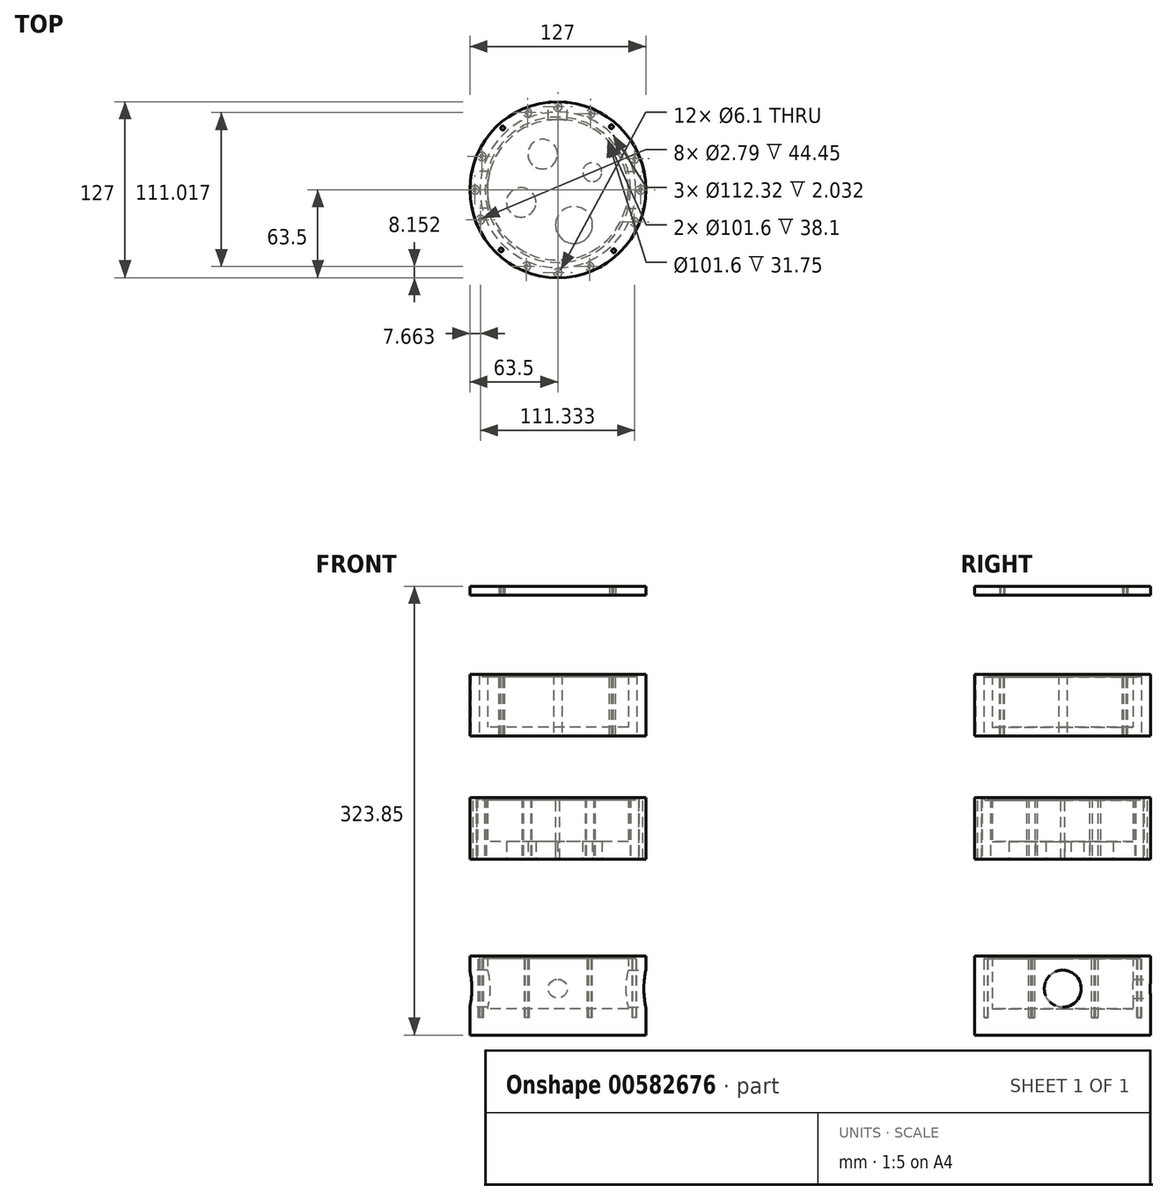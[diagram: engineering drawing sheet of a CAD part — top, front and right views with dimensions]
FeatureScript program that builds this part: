
annotation { "Feature Type Name" : "Feature", "Feature Type Description" : "" }
export const myFeature = defineFeature(function(context is Context, id is Id, definition is map)
    precondition{}
    {
        {
            var Q0;
            Q0=qCreatedBy(makeId("Top.planeOp"),FACE);
            var sketch = newSketch(context, id + "F0", { "sketchPlane" : qUnion([Q0])});
            skCircle(sketch, "E0", {"center": v(0, 0) * mm, "radius": 63.5 * mm});
            skCircle(sketch, "E1.0", {"center": v(0, 0) * mm, "radius": 50.8 * mm});
            skSolve(sketch);
        }
        {
            var Q0;
            Q0=makeQuery(id+"F0.imprint","IMPRINT",FACE,{"disambiguationData":[TD([[makeQuery(id+"F0.imprint","IMPRINT",EDGE,{"derivedFrom":sQuery(id+"F0.wireOp",EDGE,"E0")}),1.0]])]});
            extrude(context, id + "F1", {"entities" : qUnion([Q0]), "depth" : 44.45 * mm, "offsetDistance" : 25.4 * mm});
        }
        {
            var Q0;
            Q0=makeQuery(id+"F0.imprint","IMPRINT",FACE,{"disambiguationData":[TD([[makeQuery(id+"F0.imprint","IMPRINT",EDGE,{"derivedFrom":sQuery(id+"F0.wireOp",EDGE,"E1.0")}),1.0]])]});
            extrude(context, id + "F2", {"entities" : qUnion([Q0]), "operationType" : NewBodyOperationType.ADD, "depth" : 6.35 * mm, "offsetDistance" : 25.4 * mm});
        }
        {
            var Q0;
            Q0=qCreatedBy(makeId("Top.planeOp"),FACE);
            var sketch = newSketch(context, id + "F3", { "sketchPlane" : qUnion([Q0])});
            skCircle(sketch, "E2", {"center": v(0, 0) * mm, "radius": 63.5 * mm});
            skCircle(sketch, "E3.0", {"center": v(0, 0) * mm, "radius": 50.8 * mm});
            skSolve(sketch);
        }
        {
            var Q0;
            Q0=makeQuery(id+"F3.imprint","IMPRINT",FACE,{"disambiguationData":[TD([[makeQuery(id+"F3.imprint","IMPRINT",EDGE,{"derivedFrom":sQuery(id+"F3.wireOp",EDGE,"E2")}),1.0]])]});
            extrude(context, id + "F4", {"entities" : qUnion([Q0]), "operationType" : NewBodyOperationType.ADD, "depth" : 25.4 * mm, "offsetDistance" : 25.4 * mm});
        }
        {
            var Q0;
            Q0=qCreatedBy(makeId("Right.planeOp"),FACE);
            cPlane(context, id + "F5", {"entities" : qUnion([Q0]), "cplaneType" : CPlaneType.OFFSET, "offset" : 63.5 * mm, "width" : 152.4 * mm, "height" : 152.4 * mm});
        }
        {
            var Q0;
            Q0=qCreatedBy(makeId("Right.planeOp"),FACE);
            cPlane(context, id + "F6", {"entities" : qUnion([Q0]), "cplaneType" : CPlaneType.OFFSET, "offset" : 63.5 * mm, "oppositeDirection" : true, "width" : 152.4 * mm, "height" : 152.4 * mm});
        }
        {
            var Q0;
            Q0=qCreatedBy(id+"F6.planeOp",FACE);
            var sketch = newSketch(context, id + "F7", { "sketchPlane" : qUnion([Q0])});
            skCircle(sketch, "E4", {"center": v(0, 20.8) * mm, "radius": 9.53 * mm});
            skSolve(sketch);
        }
        {
            var Q0;
            Q0=qCreatedBy(id+"F5.planeOp",FACE);
            var sketch = newSketch(context, id + "F8", { "sketchPlane" : qUnion([Q0])});
            skCircle(sketch, "E5", {"center": v(0, 20.8) * mm, "radius": 9.53 * mm});
            skSolve(sketch);
        }
        {
            var Q0;
            Q0=sQuery(id+"F8.wireOp",VERTEX,"E5.center");
            var Q1;
            Q1=makeQuery(id+"F1.opExtrude","SWEPT_BODY",BODY,{"disambiguationData":[OSD([sQuery(id+"F0.wireOp",EDGE,"E0"),sQuery(id+"F0.wireOp",EDGE,"E1.0"),sQuery(id+"F0.wireOp",EDGE,"olaqje6J-RLac-xjDJ-YAwS-c4LDeK7CDQCb"),sQuery(id+"F0.wireOp",EDGE,"TtQjBYUV-K8lf-YhYr-OiMI-xCFFN7ZDIzTA"),sQuery(id+"F0.wireOp",EDGE,"TLVIDY7i-SIYg-gNVq-6KSH-QLhERAyYqyso"),sQuery(id+"F0.wireOp",EDGE,"ZflkjHLw-oWyP-XUBn-aNfn-Sa6BVqcEYZTs"),sQuery(id+"F0.wireOp",EDGE,"mPHb6uqW-qbQd-ZVMg-7JKc-ARV0pC1Ugzse"),sQuery(id+"F0.wireOp",EDGE,"s4gS2KRx-Jewy-3lGC-yEoX-xMLr9nvoNg67"),sQuery(id+"F0.wireOp",EDGE,"qZNl4cuf-riMy-4qBb-oPWZ-X3TjN7XB9Q3K"),sQuery(id+"F0.wireOp",EDGE,"BNXTqmKH-r0Qr-BDZQ-N358-95OG30awYxRb")])]});
            hole(context, id + "F9", {"style" : HoleStyle.SIMPLE, "endStyle" : HoleEndStyle.BLIND, "holeDiameter" : 26.67 * mm, "holeDepth" : 20.32 * mm, "isTappedThrough" : true, "tappedDepth" : 12.7 * mm, "tapClearance" : 3, "startFromSketch" : true, "locations" : qUnion([Q0]), "scope" : qUnion([Q1]), "majorDiameter" : 19.05 * mm});
        }
        {
            var Q0;
            Q0=sQuery(id+"F7.wireOp",VERTEX,"E4.center");
            var Q1;
            Q1=makeQuery(id+"F1.opExtrude","SWEPT_BODY",BODY,{"disambiguationData":[OSD([sQuery(id+"F0.wireOp",EDGE,"E0"),sQuery(id+"F0.wireOp",EDGE,"E1.0"),sQuery(id+"F0.wireOp",EDGE,"olaqje6J-RLac-xjDJ-YAwS-c4LDeK7CDQCb"),sQuery(id+"F0.wireOp",EDGE,"TtQjBYUV-K8lf-YhYr-OiMI-xCFFN7ZDIzTA"),sQuery(id+"F0.wireOp",EDGE,"TLVIDY7i-SIYg-gNVq-6KSH-QLhERAyYqyso"),sQuery(id+"F0.wireOp",EDGE,"ZflkjHLw-oWyP-XUBn-aNfn-Sa6BVqcEYZTs"),sQuery(id+"F0.wireOp",EDGE,"mPHb6uqW-qbQd-ZVMg-7JKc-ARV0pC1Ugzse"),sQuery(id+"F0.wireOp",EDGE,"s4gS2KRx-Jewy-3lGC-yEoX-xMLr9nvoNg67"),sQuery(id+"F0.wireOp",EDGE,"qZNl4cuf-riMy-4qBb-oPWZ-X3TjN7XB9Q3K"),sQuery(id+"F0.wireOp",EDGE,"BNXTqmKH-r0Qr-BDZQ-N358-95OG30awYxRb")])]});
            hole(context, id + "F10", {"style" : HoleStyle.SIMPLE, "endStyle" : HoleEndStyle.BLIND, "oppositeDirection" : true, "holeDiameter" : 26.67 * mm, "holeDepth" : 19.05 * mm, "isTappedThrough" : true, "tappedDepth" : 12.7 * mm, "tapClearance" : 3, "startFromSketch" : true, "locations" : qUnion([Q0]), "scope" : qUnion([Q1]), "majorDiameter" : 6.35 * mm});
        }
        {
            var Q0;
            Q0=qCreatedBy(makeId("Top.planeOp"),FACE);
            var Q1;
            Q1 = qBodyType(qCreatedBy(id + "F12" ,EDGE), BodyType.WIRE);
            cPlane(context, id + "F11", {"entities" : qUnion([Q0, Q1]), "cplaneType" : CPlaneType.OFFSET, "offset" : 114.3 * mm, "width" : 152.4 * mm, "height" : 152.4 * mm});
        }
        {
            var Q0;
            Q0=qCreatedBy(id+"F11.planeOp",FACE);
            var sketch = newSketch(context, id + "F12", { "sketchPlane" : qUnion([Q0])});
            skCircle(sketch, "E6", {"center": v(0, 0) * mm, "radius": 63.5 * mm});
            skCircle(sketch, "E7.0", {"center": v(0, 0) * mm, "radius": 50.8 * mm});
            skCircle(sketch, "E8", {"center": v(-21.95, 55.67) * mm, "radius": 3.05 * mm});
            skCircle(sketch, "E9", {"center": v(23.63, 54.98) * mm, "radius": 3.05 * mm});
            skCircle(sketch, "E10", {"center": v(55.5, 22.39) * mm, "radius": 3.05 * mm});
            skCircle(sketch, "E11", {"center": v(55.17, -23.2) * mm, "radius": 3.05 * mm});
            skCircle(sketch, "E12", {"center": v(22.83, -55.32) * mm, "radius": 3.05 * mm});
            skCircle(sketch, "E13", {"center": v(-22.75, -55.35) * mm, "radius": 3.05 * mm});
            skCircle(sketch, "E14", {"center": v(-55.84, -21.52) * mm, "radius": 3.05 * mm});
            skCircle(sketch, "E15", {"center": v(-54.8, 24.06) * mm, "radius": 3.05 * mm});
            skSolve(sketch);
        }
        {
            var Q0;
            Q0=makeQuery(id+"F12.imprint","IMPRINT",FACE,{"disambiguationData":[TD([[makeQuery(id+"F12.imprint","IMPRINT",EDGE,{"derivedFrom":sQuery(id+"F12.wireOp",EDGE,"E6")}),1.0]])]});
            extrude(context, id + "F13", {"entities" : qUnion([Q0]), "depth" : 44.45 * mm, "offsetDistance" : 25.4 * mm});
        }
        {
            var Q0;
            Q0=qCreatedBy(id+"F11.planeOp",FACE);
            var sketch = newSketch(context, id + "F14", { "sketchPlane" : qUnion([Q0])});
            skCircle(sketch, "E16", {"center": v(0, 0) * mm, "radius": 50.8 * mm});
            skSolve(sketch);
        }
        {
            var Q0;
            Q0=makeQuery(id+"F14.imprint","IMPRINT",FACE,{"disambiguationData":[TD([[makeQuery(id+"F14.imprint","IMPRINT",EDGE,{"derivedFrom":sQuery(id+"F14.wireOp",EDGE,"E16")}),1.0]])]});
            extrude(context, id + "F15", {"entities" : qUnion([Q0]), "operationType" : NewBodyOperationType.ADD, "depth" : 12.7 * mm, "offsetDistance" : 25.4 * mm});
        }
        {
            var Q0;
            Q0=qCreatedBy(id+"F11.planeOp",FACE);
            var sketch = newSketch(context, id + "F16", { "sketchPlane" : qUnion([Q0])});
            skCircle(sketch, "E17", {"center": v(-26.41, -9.1) * mm, "radius": 6.35 * mm});
            skCircle(sketch, "E18", {"center": v(-10.94, 25.7) * mm, "radius": 6.35 * mm});
            skCircle(sketch, "E19", {"center": v(24.88, 12.72) * mm, "radius": 3.18 * mm});
            skCircle(sketch, "E20", {"center": v(11.69, -25.38) * mm, "radius": 9.53 * mm});
            skSolve(sketch);
        }
        {
            var Q0;
            Q0=sQuery(id+"F16.wireOp",VERTEX,"E20.center");
            var Q1;
            Q1=makeQuery(id+"F13.opExtrude","SWEPT_BODY",BODY,{"disambiguationData":[OSD([sQuery(id+"F12.wireOp",EDGE,"E6"),sQuery(id+"F12.wireOp",EDGE,"E7.0"),sQuery(id+"F12.wireOp",EDGE,"E8"),sQuery(id+"F12.wireOp",EDGE,"E9"),sQuery(id+"F12.wireOp",EDGE,"E10"),sQuery(id+"F12.wireOp",EDGE,"E11"),sQuery(id+"F12.wireOp",EDGE,"E12"),sQuery(id+"F12.wireOp",EDGE,"E13"),sQuery(id+"F12.wireOp",EDGE,"E14"),sQuery(id+"F12.wireOp",EDGE,"E15")])]});
            hole(context, id + "F17", {"style" : HoleStyle.SIMPLE, "endStyle" : HoleEndStyle.THROUGH, "oppositeDirection" : true, "holeDiameter" : 26.67 * mm, "isTappedThrough" : true, "tappedDepth" : 12.7 * mm, "tapClearance" : 3, "startFromSketch" : true, "locations" : qUnion([Q0]), "scope" : qUnion([Q1]), "majorDiameter" : 19.05 * mm});
        }
        {
            var Q0;
            Q0=qCreatedBy(makeId("Top.planeOp"),FACE);
            cPlane(context, id + "F18", {"entities" : qUnion([Q0]), "cplaneType" : CPlaneType.OFFSET, "offset" : 203.2 * mm, "width" : 152.4 * mm, "height" : 152.4 * mm});
        }
        {
            var Q0;
            Q0=qCreatedBy(id+"F18.planeOp",FACE);
            var sketch = newSketch(context, id + "F19", { "sketchPlane" : qUnion([Q0])});
            skCircle(sketch, "E21", {"center": v(0, 0) * mm, "radius": 63.5 * mm});
            skCircle(sketch, "E22.0", {"center": v(0, 0) * mm, "radius": 50.8 * mm});
            skPoint(sketch, "E23", {"position": v(0, 59.84) * mm});
            skPoint(sketch, "E24", {"position": v(-59.84, 0) * mm});
            skPoint(sketch, "E25", {"position": v(59.84, 0) * mm});
            skPoint(sketch, "E26", {"position": v(0, -59.84) * mm});
            skSolve(sketch);
        }
        {
            var Q0;
            Q0=qCreatedBy(makeId("Front.planeOp"),FACE);
            cPlane(context, id + "F20", {"entities" : qUnion([Q0]), "cplaneType" : CPlaneType.OFFSET, "offset" : 63.5 * mm, "oppositeDirection" : true, "width" : 152.4 * mm, "height" : 152.4 * mm});
        }
        {
            var Q0;
            Q0=qCreatedBy(id+"F20.planeOp",FACE);
            var sketch = newSketch(context, id + "F21", { "sketchPlane" : qUnion([Q0])});
            skPoint(sketch, "E27", {"position": v(0, 20.8) * mm});
            skSolve(sketch);
        }
        {
            var Q0;
            Q0=sQuery(id+"F21.wireOp",VERTEX,"E27");
            var Q1;
            Q1=makeQuery(id+"F1.opExtrude","SWEPT_BODY",BODY,{"disambiguationData":[OSD([sQuery(id+"F0.wireOp",EDGE,"E0"),sQuery(id+"F0.wireOp",EDGE,"E1.0"),sQuery(id+"F0.wireOp",EDGE,"olaqje6J-RLac-xjDJ-YAwS-c4LDeK7CDQCb"),sQuery(id+"F0.wireOp",EDGE,"TtQjBYUV-K8lf-YhYr-OiMI-xCFFN7ZDIzTA"),sQuery(id+"F0.wireOp",EDGE,"TLVIDY7i-SIYg-gNVq-6KSH-QLhERAyYqyso"),sQuery(id+"F0.wireOp",EDGE,"ZflkjHLw-oWyP-XUBn-aNfn-Sa6BVqcEYZTs"),sQuery(id+"F0.wireOp",EDGE,"mPHb6uqW-qbQd-ZVMg-7JKc-ARV0pC1Ugzse"),sQuery(id+"F0.wireOp",EDGE,"s4gS2KRx-Jewy-3lGC-yEoX-xMLr9nvoNg67"),sQuery(id+"F0.wireOp",EDGE,"qZNl4cuf-riMy-4qBb-oPWZ-X3TjN7XB9Q3K"),sQuery(id+"F0.wireOp",EDGE,"BNXTqmKH-r0Qr-BDZQ-N358-95OG30awYxRb")])]});
            hole(context, id + "F22", {"style" : HoleStyle.SIMPLE, "endStyle" : HoleEndStyle.BLIND, "oppositeDirection" : true, "holeDiameter" : 13.72 * mm, "majorDiameter" : 5 * mm, "holeDepth" : 15.42 * mm, "isTappedThrough" : true, "tappedDepth" : 12.7 * mm, "tapClearance" : 3, "startFromSketch" : true, "locations" : qUnion([Q0]), "scope" : qUnion([Q1])});
        }
        {
            var Q0;
            Q0=qCreatedBy(id+"F18.planeOp",FACE);
            var sketch = newSketch(context, id + "F23", { "sketchPlane" : qUnion([Q0])});
            skCircle(sketch, "E28", {"center": v(0, 0) * mm, "radius": 50.8 * mm});
            skSolve(sketch);
        }
        {
            var Q0;
            Q0=qCreatedBy(id+"F18.planeOp",FACE);
            cPlane(context, id + "F24", {"entities" : qUnion([Q0]), "cplaneType" : CPlaneType.OFFSET, "offset" : 101.6 * mm, "width" : 152.4 * mm, "height" : 152.4 * mm});
        }
        {
            var Q0;
            Q0=qCreatedBy(id+"F24.planeOp",FACE);
            var sketch = newSketch(context, id + "F25", { "sketchPlane" : qUnion([Q0])});
            skCircle(sketch, "E29", {"center": v(0, 0) * mm, "radius": 63.5 * mm});
            skPoint(sketch, "E30", {"position": v(-39.76, 44.52) * mm});
            skPoint(sketch, "E31", {"position": v(-40.96, -43.42) * mm});
            skPoint(sketch, "E32", {"position": v(40.34, -44) * mm});
            skPoint(sketch, "E33", {"position": v(38.66, 45.48) * mm});
            skSolve(sketch);
        }
        {
            var Q0;
            Q0=makeQuery(id+"F25.imprint","IMPRINT",FACE,{"disambiguationData":[TD([[makeQuery(id+"F25.imprint","IMPRINT",EDGE,{"derivedFrom":sQuery(id+"F25.wireOp",EDGE,"E29")}),1.0]])]});
            extrude(context, id + "F26", {"entities" : qUnion([Q0]), "depth" : 6.35 * mm, "offsetDistance" : 25.4 * mm});
        }
        {
            var Q0;
            Q0=sQuery(id+"F19.wireOp",VERTEX,"E23");
            var Q1;
            Q1=makeQuery(id+"F13.opExtrude","SWEPT_BODY",BODY,{"disambiguationData":[OSD([sQuery(id+"F12.wireOp",EDGE,"E6"),sQuery(id+"F12.wireOp",EDGE,"E7.0"),sQuery(id+"F12.wireOp",EDGE,"E8"),sQuery(id+"F12.wireOp",EDGE,"E9"),sQuery(id+"F12.wireOp",EDGE,"E10"),sQuery(id+"F12.wireOp",EDGE,"E11"),sQuery(id+"F12.wireOp",EDGE,"E12"),sQuery(id+"F12.wireOp",EDGE,"E13"),sQuery(id+"F12.wireOp",EDGE,"E14"),sQuery(id+"F12.wireOp",EDGE,"E15")])]});
            hole(context, id + "F27", {"style" : HoleStyle.SIMPLE, "endStyle" : HoleEndStyle.THROUGH, "holeDiameter" : 2.8 * mm, "majorDiameter" : 6.35 * mm, "isTappedThrough" : true, "tappedDepth" : 12.7 * mm, "tapClearance" : 3, "startFromSketch" : true, "locations" : qUnion([Q0]), "scope" : qUnion([Q1])});
        }
        {
            var Q0;
            Q0=sQuery(id+"F25.wireOp",VERTEX,"E30");
            var Q1;
            Q1=makeQuery(id+"F26.opExtrude","SWEPT_BODY",BODY,{"disambiguationData":[OSD([sQuery(id+"F25.wireOp",EDGE,"E29")])]});
            hole(context, id + "F28", {"style" : HoleStyle.SIMPLE, "endStyle" : HoleEndStyle.THROUGH, "oppositeDirection" : true, "holeDiameter" : 2.8 * mm, "majorDiameter" : 6.35 * mm, "isTappedThrough" : true, "tappedDepth" : 12.7 * mm, "tapClearance" : 3, "startFromSketch" : true, "locations" : qUnion([Q0]), "scope" : qUnion([Q1])});
        }
        {
            var Q0;
            Q0=makeQuery(id+"F19.imprint","IMPRINT",FACE,{"disambiguationData":[TD([[makeQuery(id+"F19.imprint","IMPRINT",EDGE,{"derivedFrom":sQuery(id+"F19.wireOp",EDGE,"E21")}),1.0]])]});
            extrude(context, id + "F29", {"entities" : qUnion([Q0]), "depth" : 44.45 * mm, "offsetDistance" : 25.4 * mm});
        }
        {
            var Q0;
            Q0=makeQuery(id+"F23.imprint","IMPRINT",FACE,{"disambiguationData":[TD([[makeQuery(id+"F23.imprint","IMPRINT",EDGE,{"derivedFrom":sQuery(id+"F23.wireOp",EDGE,"E28")}),1.0]])]});
            extrude(context, id + "F30", {"entities" : qUnion([Q0]), "operationType" : NewBodyOperationType.ADD, "depth" : 6.35 * mm, "offsetDistance" : 25.4 * mm});
        }
        {
            var Q0;
            Q0=qCreatedBy(makeId("Top.planeOp"),FACE);
            cPlane(context, id + "F31", {"entities" : qUnion([Q0]), "cplaneType" : CPlaneType.OFFSET, "offset" : 44.45 * mm, "width" : 152.4 * mm, "height" : 152.4 * mm});
        }
        {
            var Q0;
            Q0=qCreatedBy(id+"F31.planeOp",FACE);
            var sketch = newSketch(context, id + "F32", { "sketchPlane" : qUnion([Q0])});
            skPoint(sketch, "E34", {"position": v(55.17, -23.2) * mm});
            skPoint(sketch, "E35", {"position": v(22.83, -55.32) * mm});
            skPoint(sketch, "E36", {"position": v(-22.75, -55.35) * mm});
            skPoint(sketch, "E37", {"position": v(-55.84, -21.52) * mm});
            skPoint(sketch, "E38", {"position": v(-54.8, 24.06) * mm});
            skPoint(sketch, "E39", {"position": v(-21.95, 55.67) * mm});
            skPoint(sketch, "E40", {"position": v(23.63, 54.98) * mm});
            skPoint(sketch, "E41", {"position": v(55.5, 22.39) * mm});
            skSolve(sketch);
        }
        {
            var Q0;
            Q0=sQuery(id+"F32.wireOp",VERTEX,"E37");
            var Q1;
            Q1=makeQuery(id+"F1.opExtrude","SWEPT_BODY",BODY,{"disambiguationData":[OSD([sQuery(id+"F0.wireOp",EDGE,"E0"),sQuery(id+"F0.wireOp",EDGE,"E1.0")])]});
            hole(context, id + "F33", {"style" : HoleStyle.SIMPLE, "endStyle" : HoleEndStyle.THROUGH, "holeDiameter" : 2.8 * mm, "majorDiameter" : 6.35 * mm, "isTappedThrough" : true, "tappedDepth" : 12.7 * mm, "tapClearance" : 3, "startFromSketch" : true, "locations" : qUnion([Q0]), "scope" : qUnion([Q1])});
        }
        {
            var Q0;
            Q0=sQuery(id+"F32.wireOp",VERTEX,"E36");
            var Q1;
            Q1=makeQuery(id+"F1.opExtrude","SWEPT_BODY",BODY,{"disambiguationData":[OSD([sQuery(id+"F0.wireOp",EDGE,"E0"),sQuery(id+"F0.wireOp",EDGE,"E1.0")])]});
            hole(context, id + "F34", {"style" : HoleStyle.SIMPLE, "endStyle" : HoleEndStyle.THROUGH, "holeDiameter" : 2.8 * mm, "majorDiameter" : 6.35 * mm, "isTappedThrough" : true, "tappedDepth" : 12.7 * mm, "tapClearance" : 3, "startFromSketch" : true, "locations" : qUnion([Q0]), "scope" : qUnion([Q1])});
        }
        {
            var Q0;
            Q0=sQuery(id+"F32.wireOp",VERTEX,"E38");
            var Q1;
            Q1=makeQuery(id+"F1.opExtrude","SWEPT_BODY",BODY,{"disambiguationData":[OSD([sQuery(id+"F0.wireOp",EDGE,"E0"),sQuery(id+"F0.wireOp",EDGE,"E1.0")])]});
            hole(context, id + "F35", {"style" : HoleStyle.SIMPLE, "endStyle" : HoleEndStyle.THROUGH, "holeDiameter" : 2.8 * mm, "majorDiameter" : 6.35 * mm, "isTappedThrough" : true, "tappedDepth" : 12.7 * mm, "tapClearance" : 3, "startFromSketch" : true, "locations" : qUnion([Q0]), "scope" : qUnion([Q1])});
        }
        {
            var Q0;
            Q0=sQuery(id+"F32.wireOp",VERTEX,"E39");
            var Q1;
            Q1=makeQuery(id+"F1.opExtrude","SWEPT_BODY",BODY,{"disambiguationData":[OSD([sQuery(id+"F0.wireOp",EDGE,"E0"),sQuery(id+"F0.wireOp",EDGE,"E1.0")])]});
            hole(context, id + "F36", {"style" : HoleStyle.SIMPLE, "endStyle" : HoleEndStyle.THROUGH, "holeDiameter" : 2.8 * mm, "majorDiameter" : 6.35 * mm, "isTappedThrough" : true, "tappedDepth" : 12.7 * mm, "tapClearance" : 3, "startFromSketch" : true, "locations" : qUnion([Q0]), "scope" : qUnion([Q1])});
        }
        {
            var Q0;
            Q0=sQuery(id+"F32.wireOp",VERTEX,"E40");
            var Q1;
            Q1=makeQuery(id+"F1.opExtrude","SWEPT_BODY",BODY,{"disambiguationData":[OSD([sQuery(id+"F0.wireOp",EDGE,"E0"),sQuery(id+"F0.wireOp",EDGE,"E1.0")])]});
            hole(context, id + "F37", {"style" : HoleStyle.SIMPLE, "endStyle" : HoleEndStyle.THROUGH, "holeDiameter" : 2.8 * mm, "majorDiameter" : 6.35 * mm, "isTappedThrough" : true, "tappedDepth" : 12.7 * mm, "tapClearance" : 3, "startFromSketch" : true, "locations" : qUnion([Q0]), "scope" : qUnion([Q1])});
        }
        {
            var Q0;
            Q0=sQuery(id+"F32.wireOp",VERTEX,"E41");
            var Q1;
            Q1=makeQuery(id+"F1.opExtrude","SWEPT_BODY",BODY,{"disambiguationData":[OSD([sQuery(id+"F0.wireOp",EDGE,"E0"),sQuery(id+"F0.wireOp",EDGE,"E1.0")])]});
            hole(context, id + "F38", {"style" : HoleStyle.SIMPLE, "endStyle" : HoleEndStyle.THROUGH, "holeDiameter" : 2.8 * mm, "majorDiameter" : 6.35 * mm, "isTappedThrough" : true, "tappedDepth" : 12.7 * mm, "tapClearance" : 3, "startFromSketch" : true, "locations" : qUnion([Q0]), "scope" : qUnion([Q1])});
        }
        {
            var Q0;
            Q0=sQuery(id+"F32.wireOp",VERTEX,"E34");
            var Q1;
            Q1=makeQuery(id+"F1.opExtrude","SWEPT_BODY",BODY,{"disambiguationData":[OSD([sQuery(id+"F0.wireOp",EDGE,"E0"),sQuery(id+"F0.wireOp",EDGE,"E1.0")])]});
            hole(context, id + "F39", {"style" : HoleStyle.SIMPLE, "endStyle" : HoleEndStyle.THROUGH, "holeDiameter" : 2.8 * mm, "majorDiameter" : 6.35 * mm, "isTappedThrough" : true, "tappedDepth" : 12.7 * mm, "tapClearance" : 3, "startFromSketch" : true, "locations" : qUnion([Q0]), "scope" : qUnion([Q1])});
        }
        {
            var Q0;
            Q0=sQuery(id+"F32.wireOp",VERTEX,"E35");
            var Q1;
            Q1=makeQuery(id+"F1.opExtrude","SWEPT_BODY",BODY,{"disambiguationData":[OSD([sQuery(id+"F0.wireOp",EDGE,"E0"),sQuery(id+"F0.wireOp",EDGE,"E1.0")])]});
            hole(context, id + "F40", {"style" : HoleStyle.SIMPLE, "endStyle" : HoleEndStyle.THROUGH, "holeDiameter" : 2.8 * mm, "majorDiameter" : 6.35 * mm, "isTappedThrough" : true, "tappedDepth" : 12.7 * mm, "tapClearance" : 3, "startFromSketch" : true, "locations" : qUnion([Q0]), "scope" : qUnion([Q1])});
        }
        {
            var Q0;
            Q0=qCreatedBy(id+"F31.planeOp",FACE);
            var sketch = newSketch(context, id + "F41", { "sketchPlane" : qUnion([Q0])});
            skCircle(sketch, "E42", {"center": v(0, 0) * mm, "radius": 52.48 * mm});
            skCircle(sketch, "E43", {"center": v(0, 0) * mm, "radius": 56.16 * mm});
            skSolve(sketch);
        }
        {
            var Q0;
            Q0 = qSketchRegion(id + "F41", true);
            extrude(context, id + "F42", {"entities" : qUnion([Q0]), "operationType" : NewBodyOperationType.REMOVE, "oppositeDirection" : true, "depth" : 2.03 * mm, "offsetDistance" : 25.4 * mm});
        }
        {
            var Q0;
            Q0=qCreatedBy(id+"F11.planeOp",FACE);
            cPlane(context, id + "F43", {"entities" : qUnion([Q0]), "cplaneType" : CPlaneType.OFFSET, "offset" : 44.45 * mm, "width" : 152.4 * mm, "height" : 152.4 * mm});
        }
        {
            var Q0;
            Q0=qCreatedBy(id+"F43.planeOp",FACE);
            var sketch = newSketch(context, id + "F44", { "sketchPlane" : qUnion([Q0])});
            skCircle(sketch, "E44", {"center": v(0, 0) * mm, "radius": 52.48 * mm});
            skCircle(sketch, "E45", {"center": v(0, 0) * mm, "radius": 56.16 * mm});
            skSolve(sketch);
        }
        {
            var Q0;
            Q0=makeQuery(id+"F44.imprint","IMPRINT",FACE,{"disambiguationData":[TD([[makeQuery(id+"F44.imprint","IMPRINT",EDGE,{"derivedFrom":sQuery(id+"F44.wireOp",EDGE,"E44")}),-1.0]])]});
            extrude(context, id + "F45", {"entities" : qUnion([Q0]), "operationType" : NewBodyOperationType.REMOVE, "oppositeDirection" : true, "depth" : 2.03 * mm, "offsetDistance" : 25.4 * mm});
        }
        {
            var Q0;
            Q0=qCreatedBy(id+"F18.planeOp",FACE);
            cPlane(context, id + "F46", {"entities" : qUnion([Q0]), "cplaneType" : CPlaneType.OFFSET, "offset" : 44.45 * mm, "width" : 152.4 * mm, "height" : 152.4 * mm});
        }
        {
            var Q0;
            Q0=qCreatedBy(id+"F46.planeOp",FACE);
            var sketch = newSketch(context, id + "F47", { "sketchPlane" : qUnion([Q0])});
            skCircle(sketch, "E46", {"center": v(0, 0) * mm, "radius": 52.48 * mm});
            skCircle(sketch, "E47", {"center": v(0, 0) * mm, "radius": 56.16 * mm});
            skSolve(sketch);
        }
        {
            var Q0;
            Q0=makeQuery(id+"F47.imprint","IMPRINT",FACE,{"disambiguationData":[TD([[makeQuery(id+"F47.imprint","IMPRINT",EDGE,{"derivedFrom":sQuery(id+"F47.wireOp",EDGE,"E46")}),-1.0]])]});
            extrude(context, id + "F48", {"entities" : qUnion([Q0]), "operationType" : NewBodyOperationType.REMOVE, "oppositeDirection" : true, "depth" : 2.03 * mm, "offsetDistance" : 25.4 * mm});
        }
        {
            var Q0;
            Q0=sQuery(id+"F19.wireOp",VERTEX,"E26");
            var Q1;
            Q1=makeQuery(id+"F13.opExtrude","SWEPT_BODY",BODY,{"disambiguationData":[OSD([sQuery(id+"F12.wireOp",EDGE,"E6"),sQuery(id+"F12.wireOp",EDGE,"E7.0"),sQuery(id+"F12.wireOp",EDGE,"E8"),sQuery(id+"F12.wireOp",EDGE,"E9"),sQuery(id+"F12.wireOp",EDGE,"E10"),sQuery(id+"F12.wireOp",EDGE,"E11"),sQuery(id+"F12.wireOp",EDGE,"E12"),sQuery(id+"F12.wireOp",EDGE,"E13"),sQuery(id+"F12.wireOp",EDGE,"E14"),sQuery(id+"F12.wireOp",EDGE,"E15")])]});
            hole(context, id + "F49", {"style" : HoleStyle.SIMPLE, "endStyle" : HoleEndStyle.THROUGH, "holeDiameter" : 2.8 * mm, "majorDiameter" : 6.35 * mm, "isTappedThrough" : true, "tappedDepth" : 12.7 * mm, "tapClearance" : 3, "startFromSketch" : true, "locations" : qUnion([Q0]), "scope" : qUnion([Q1])});
        }
        {
            var Q0;
            Q0=sQuery(id+"F19.wireOp",VERTEX,"E26");
            var Q1;
            Q1=makeQuery(id+"F29.opExtrude","SWEPT_BODY",BODY,{"disambiguationData":[OSD([sQuery(id+"F19.wireOp",EDGE,"E21"),sQuery(id+"F19.wireOp",EDGE,"E22.0")])]});
            hole(context, id + "F50", {"style" : HoleStyle.SIMPLE, "endStyle" : HoleEndStyle.THROUGH, "oppositeDirection" : true, "holeDiameter" : 6.1 * mm, "majorDiameter" : 6.35 * mm, "isTappedThrough" : true, "tappedDepth" : 12.7 * mm, "tapClearance" : 3, "startFromSketch" : true, "locations" : qUnion([Q0]), "scope" : qUnion([Q1])});
        }
        {
            var Q0;
            Q0=sQuery(id+"F19.wireOp",VERTEX,"E25");
            var Q1;
            Q1=makeQuery(id+"F13.opExtrude","SWEPT_BODY",BODY,{"disambiguationData":[OSD([sQuery(id+"F12.wireOp",EDGE,"E6"),sQuery(id+"F12.wireOp",EDGE,"E7.0"),sQuery(id+"F12.wireOp",EDGE,"E8"),sQuery(id+"F12.wireOp",EDGE,"E9"),sQuery(id+"F12.wireOp",EDGE,"E10"),sQuery(id+"F12.wireOp",EDGE,"E11"),sQuery(id+"F12.wireOp",EDGE,"E12"),sQuery(id+"F12.wireOp",EDGE,"E13"),sQuery(id+"F12.wireOp",EDGE,"E14"),sQuery(id+"F12.wireOp",EDGE,"E15")])]});
            hole(context, id + "F51", {"style" : HoleStyle.SIMPLE, "endStyle" : HoleEndStyle.THROUGH, "holeDiameter" : 2.8 * mm, "majorDiameter" : 6.35 * mm, "isTappedThrough" : true, "tappedDepth" : 12.7 * mm, "tapClearance" : 3, "startFromSketch" : true, "locations" : qUnion([Q0]), "scope" : qUnion([Q1])});
        }
        {
            var Q0;
            Q0=sQuery(id+"F19.wireOp",VERTEX,"E25");
            var Q1;
            Q1=makeQuery(id+"F29.opExtrude","SWEPT_BODY",BODY,{"disambiguationData":[OSD([sQuery(id+"F19.wireOp",EDGE,"E21"),sQuery(id+"F19.wireOp",EDGE,"E22.0")])]});
            hole(context, id + "F52", {"style" : HoleStyle.SIMPLE, "endStyle" : HoleEndStyle.THROUGH, "oppositeDirection" : true, "holeDiameter" : 6.1 * mm, "majorDiameter" : 6.35 * mm, "isTappedThrough" : true, "tappedDepth" : 12.7 * mm, "tapClearance" : 3, "startFromSketch" : true, "locations" : qUnion([Q0]), "scope" : qUnion([Q1])});
        }
        {
            var Q0;
            Q0=sQuery(id+"F19.wireOp",VERTEX,"E23");
            var Q1;
            Q1=makeQuery(id+"F29.opExtrude","SWEPT_BODY",BODY,{"disambiguationData":[OSD([sQuery(id+"F19.wireOp",EDGE,"E21"),sQuery(id+"F19.wireOp",EDGE,"E22.0")])]});
            hole(context, id + "F53", {"style" : HoleStyle.SIMPLE, "endStyle" : HoleEndStyle.THROUGH, "oppositeDirection" : true, "holeDiameter" : 6.1 * mm, "majorDiameter" : 6.35 * mm, "isTappedThrough" : true, "tappedDepth" : 12.7 * mm, "tapClearance" : 3, "startFromSketch" : true, "locations" : qUnion([Q0]), "scope" : qUnion([Q1])});
        }
        {
            var Q0;
            Q0=sQuery(id+"F19.wireOp",VERTEX,"E24");
            var Q1;
            Q1=makeQuery(id+"F29.opExtrude","SWEPT_BODY",BODY,{"disambiguationData":[OSD([sQuery(id+"F19.wireOp",EDGE,"E21"),sQuery(id+"F19.wireOp",EDGE,"E22.0")])]});
            hole(context, id + "F54", {"style" : HoleStyle.SIMPLE, "endStyle" : HoleEndStyle.THROUGH, "oppositeDirection" : true, "holeDiameter" : 6.1 * mm, "majorDiameter" : 6.35 * mm, "isTappedThrough" : true, "tappedDepth" : 12.7 * mm, "tapClearance" : 3, "startFromSketch" : true, "locations" : qUnion([Q0]), "scope" : qUnion([Q1])});
        }
        {
            var Q0;
            Q0=sQuery(id+"F19.wireOp",VERTEX,"E24");
            var Q1;
            Q1=makeQuery(id+"F13.opExtrude","SWEPT_BODY",BODY,{"disambiguationData":[OSD([sQuery(id+"F12.wireOp",EDGE,"E6"),sQuery(id+"F12.wireOp",EDGE,"E7.0"),sQuery(id+"F12.wireOp",EDGE,"E8"),sQuery(id+"F12.wireOp",EDGE,"E9"),sQuery(id+"F12.wireOp",EDGE,"E10"),sQuery(id+"F12.wireOp",EDGE,"E11"),sQuery(id+"F12.wireOp",EDGE,"E12"),sQuery(id+"F12.wireOp",EDGE,"E13"),sQuery(id+"F12.wireOp",EDGE,"E14"),sQuery(id+"F12.wireOp",EDGE,"E15")])]});
            hole(context, id + "F55", {"style" : HoleStyle.SIMPLE, "endStyle" : HoleEndStyle.THROUGH, "holeDiameter" : 2.8 * mm, "majorDiameter" : 6.35 * mm, "isTappedThrough" : true, "tappedDepth" : 12.7 * mm, "tapClearance" : 3, "startFromSketch" : true, "locations" : qUnion([Q0]), "scope" : qUnion([Q1])});
        }
        {
            var Q0;
            Q0=sQuery(id+"F25.wireOp",VERTEX,"E30");
            var Q1;
            Q1=makeQuery(id+"F29.opExtrude","SWEPT_BODY",BODY,{"disambiguationData":[OSD([sQuery(id+"F19.wireOp",EDGE,"E21"),sQuery(id+"F19.wireOp",EDGE,"E22.0")])]});
            hole(context, id + "F56", {"style" : HoleStyle.SIMPLE, "endStyle" : HoleEndStyle.THROUGH, "holeDiameter" : 2.8 * mm, "majorDiameter" : 6.35 * mm, "isTappedThrough" : true, "tappedDepth" : 12.7 * mm, "tapClearance" : 3, "startFromSketch" : true, "locations" : qUnion([Q0]), "scope" : qUnion([Q1])});
        }
        {
            var Q0;
            Q0=sQuery(id+"F25.wireOp",VERTEX,"E31");
            var Q1;
            Q1=makeQuery(id+"F26.opExtrude","SWEPT_BODY",BODY,{"disambiguationData":[OSD([sQuery(id+"F25.wireOp",EDGE,"E29")])]});
            hole(context, id + "F57", {"style" : HoleStyle.SIMPLE, "endStyle" : HoleEndStyle.THROUGH, "oppositeDirection" : true, "holeDiameter" : 2.8 * mm, "majorDiameter" : 6.35 * mm, "isTappedThrough" : true, "tappedDepth" : 12.7 * mm, "tapClearance" : 3, "startFromSketch" : true, "locations" : qUnion([Q0]), "scope" : qUnion([Q1])});
        }
        {
            var Q0;
            Q0=sQuery(id+"F25.wireOp",VERTEX,"E31");
            var Q1;
            Q1=makeQuery(id+"F29.opExtrude","SWEPT_BODY",BODY,{"disambiguationData":[OSD([sQuery(id+"F19.wireOp",EDGE,"E21"),sQuery(id+"F19.wireOp",EDGE,"E22.0")])]});
            hole(context, id + "F58", {"style" : HoleStyle.SIMPLE, "endStyle" : HoleEndStyle.THROUGH, "holeDiameter" : 2.8 * mm, "majorDiameter" : 6.35 * mm, "isTappedThrough" : true, "tappedDepth" : 12.7 * mm, "tapClearance" : 3, "startFromSketch" : true, "locations" : qUnion([Q0]), "scope" : qUnion([Q1])});
        }
        {
            var Q0;
            Q0=sQuery(id+"F25.wireOp",VERTEX,"E32");
            var Q1;
            Q1=makeQuery(id+"F29.opExtrude","SWEPT_BODY",BODY,{"disambiguationData":[OSD([sQuery(id+"F19.wireOp",EDGE,"E21"),sQuery(id+"F19.wireOp",EDGE,"E22.0")])]});
            hole(context, id + "F59", {"style" : HoleStyle.SIMPLE, "endStyle" : HoleEndStyle.THROUGH, "holeDiameter" : 2.8 * mm, "majorDiameter" : 6.35 * mm, "isTappedThrough" : true, "tappedDepth" : 12.7 * mm, "tapClearance" : 3, "startFromSketch" : true, "locations" : qUnion([Q0]), "scope" : qUnion([Q1])});
        }
        {
            var Q0;
            Q0=sQuery(id+"F25.wireOp",VERTEX,"E32");
            var Q1;
            Q1=makeQuery(id+"F26.opExtrude","SWEPT_BODY",BODY,{"disambiguationData":[OSD([sQuery(id+"F25.wireOp",EDGE,"E29")])]});
            hole(context, id + "F60", {"style" : HoleStyle.SIMPLE, "endStyle" : HoleEndStyle.THROUGH, "oppositeDirection" : true, "holeDiameter" : 2.8 * mm, "majorDiameter" : 6.35 * mm, "isTappedThrough" : true, "tappedDepth" : 12.7 * mm, "tapClearance" : 3, "startFromSketch" : true, "locations" : qUnion([Q0]), "scope" : qUnion([Q1])});
        }
        {
            var Q0;
            Q0=sQuery(id+"F25.wireOp",VERTEX,"E33");
            var Q1;
            Q1=makeQuery(id+"F26.opExtrude","SWEPT_BODY",BODY,{"disambiguationData":[OSD([sQuery(id+"F25.wireOp",EDGE,"E29")])]});
            hole(context, id + "F61", {"style" : HoleStyle.SIMPLE, "endStyle" : HoleEndStyle.THROUGH, "oppositeDirection" : true, "holeDiameter" : 2.8 * mm, "majorDiameter" : 6.35 * mm, "isTappedThrough" : true, "tappedDepth" : 12.7 * mm, "tapClearance" : 3, "startFromSketch" : true, "locations" : qUnion([Q0]), "scope" : qUnion([Q1])});
        }
        {
            var Q0;
            Q0=sQuery(id+"F25.wireOp",VERTEX,"E33");
            var Q1;
            Q1=makeQuery(id+"F29.opExtrude","SWEPT_BODY",BODY,{"disambiguationData":[OSD([sQuery(id+"F19.wireOp",EDGE,"E21"),sQuery(id+"F19.wireOp",EDGE,"E22.0")])]});
            hole(context, id + "F62", {"style" : HoleStyle.SIMPLE, "endStyle" : HoleEndStyle.THROUGH, "holeDiameter" : 2.8 * mm, "majorDiameter" : 6.35 * mm, "isTappedThrough" : true, "tappedDepth" : 12.7 * mm, "tapClearance" : 3, "startFromSketch" : true, "locations" : qUnion([Q0]), "scope" : qUnion([Q1])});
        }
        {
            var Q0;
            Q0=sQuery(id+"F16.wireOp",VERTEX,"E17.center");
            var Q1;
            Q1=makeQuery(id+"F13.opExtrude","SWEPT_BODY",BODY,{"disambiguationData":[OSD([sQuery(id+"F12.wireOp",EDGE,"E6"),sQuery(id+"F12.wireOp",EDGE,"E7.0"),sQuery(id+"F12.wireOp",EDGE,"E8"),sQuery(id+"F12.wireOp",EDGE,"E9"),sQuery(id+"F12.wireOp",EDGE,"E10"),sQuery(id+"F12.wireOp",EDGE,"E11"),sQuery(id+"F12.wireOp",EDGE,"E12"),sQuery(id+"F12.wireOp",EDGE,"E13"),sQuery(id+"F12.wireOp",EDGE,"E14"),sQuery(id+"F12.wireOp",EDGE,"E15")])]});
            hole(context, id + "F63", {"style" : HoleStyle.SIMPLE, "endStyle" : HoleEndStyle.THROUGH, "oppositeDirection" : true, "holeDiameter" : 21.34 * mm, "majorDiameter" : 6.35 * mm, "isTappedThrough" : true, "tappedDepth" : 12.7 * mm, "tapClearance" : 3, "startFromSketch" : true, "locations" : qUnion([Q0]), "scope" : qUnion([Q1])});
        }
        {
            var Q0;
            Q0=sQuery(id+"F16.wireOp",VERTEX,"E18.center");
            var Q1;
            Q1=makeQuery(id+"F13.opExtrude","SWEPT_BODY",BODY,{"disambiguationData":[OSD([sQuery(id+"F12.wireOp",EDGE,"E6"),sQuery(id+"F12.wireOp",EDGE,"E7.0"),sQuery(id+"F12.wireOp",EDGE,"E8"),sQuery(id+"F12.wireOp",EDGE,"E9"),sQuery(id+"F12.wireOp",EDGE,"E10"),sQuery(id+"F12.wireOp",EDGE,"E11"),sQuery(id+"F12.wireOp",EDGE,"E12"),sQuery(id+"F12.wireOp",EDGE,"E13"),sQuery(id+"F12.wireOp",EDGE,"E14"),sQuery(id+"F12.wireOp",EDGE,"E15")])]});
            hole(context, id + "F64", {"style" : HoleStyle.SIMPLE, "endStyle" : HoleEndStyle.THROUGH, "oppositeDirection" : true, "holeDiameter" : 21.34 * mm, "majorDiameter" : 6.35 * mm, "isTappedThrough" : true, "tappedDepth" : 12.7 * mm, "tapClearance" : 3, "startFromSketch" : true, "locations" : qUnion([Q0]), "scope" : qUnion([Q1])});
        }
        {
            var Q0;
            Q0=sQuery(id+"F16.wireOp",VERTEX,"E19.center");
            var Q1;
            Q1=makeQuery(id+"F13.opExtrude","SWEPT_BODY",BODY,{"disambiguationData":[OSD([sQuery(id+"F12.wireOp",EDGE,"E6"),sQuery(id+"F12.wireOp",EDGE,"E7.0"),sQuery(id+"F12.wireOp",EDGE,"E8"),sQuery(id+"F12.wireOp",EDGE,"E9"),sQuery(id+"F12.wireOp",EDGE,"E10"),sQuery(id+"F12.wireOp",EDGE,"E11"),sQuery(id+"F12.wireOp",EDGE,"E12"),sQuery(id+"F12.wireOp",EDGE,"E13"),sQuery(id+"F12.wireOp",EDGE,"E14"),sQuery(id+"F12.wireOp",EDGE,"E15")])]});
            hole(context, id + "F65", {"style" : HoleStyle.SIMPLE, "endStyle" : HoleEndStyle.THROUGH, "oppositeDirection" : true, "holeDiameter" : 13.72 * mm, "majorDiameter" : 6.35 * mm, "isTappedThrough" : true, "tappedDepth" : 12.7 * mm, "tapClearance" : 3, "startFromSketch" : true, "locations" : qUnion([Q0]), "scope" : qUnion([Q1])});
        }
        {
            var Q0;
            Q0=makeQuery(id+"F0.imprint","IMPRINT",FACE,{"disambiguationData":[TD([[makeQuery(id+"F0.imprint","IMPRINT",EDGE,{"derivedFrom":sQuery(id+"F0.wireOp",EDGE,"E0")}),1.0]])]});
            var Q1;
            Q1=makeQuery(id+"F0.imprint","IMPRINT",FACE,{"disambiguationData":[TD([[makeQuery(id+"F0.imprint","IMPRINT",EDGE,{"derivedFrom":sQuery(id+"F0.wireOp",EDGE,"E1.0")}),1.0]])]});
            extrude(context, id + "F66", {"entities" : qUnion([Q0, Q1]), "operationType" : NewBodyOperationType.ADD, "oppositeDirection" : true, "depth" : 12.7 * mm, "offsetDistance" : 25.4 * mm});
        }
    });
